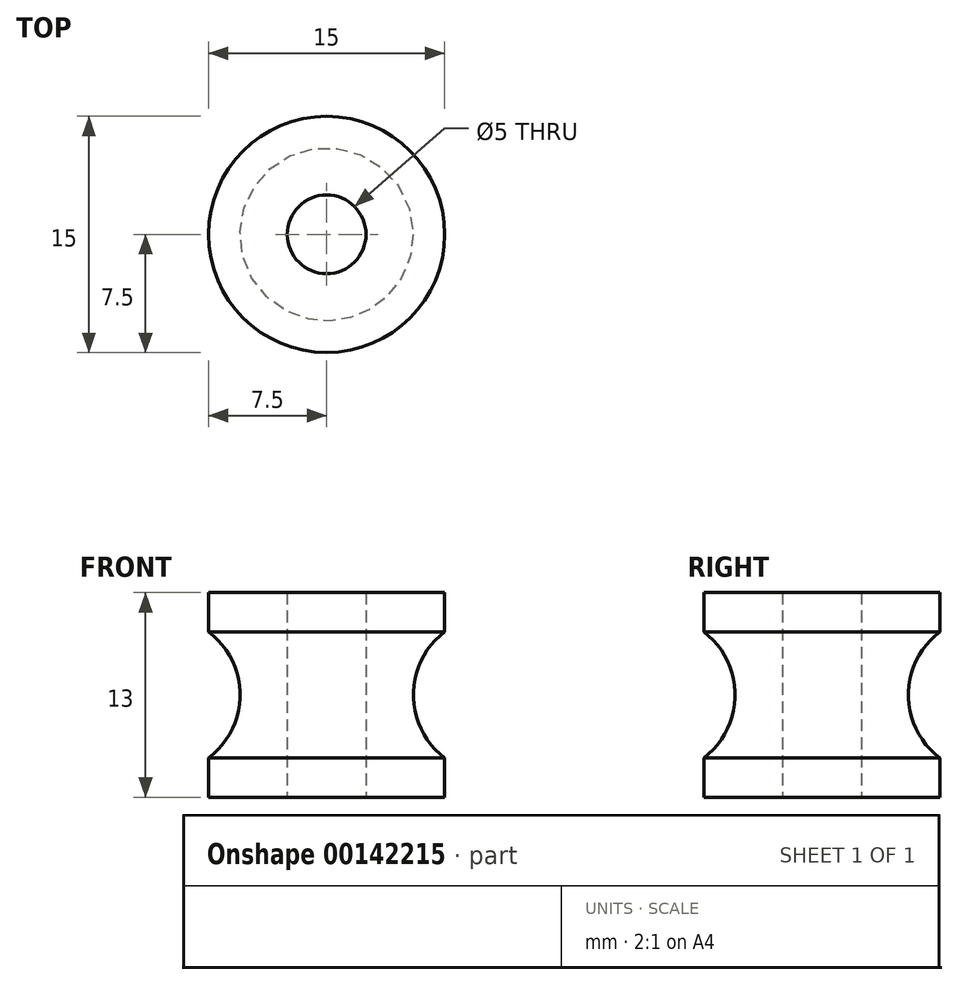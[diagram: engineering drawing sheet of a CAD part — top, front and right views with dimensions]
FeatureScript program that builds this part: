
annotation { "Feature Type Name" : "Feature", "Feature Type Description" : "" }
export const myFeature = defineFeature(function(context is Context, id is Id, definition is map)
    precondition{}
    {
        {
            var Q0;
            Q0=qCreatedBy(makeId("Top.planeOp"),FACE);
            var sketch = newSketch(context, id + "F0", { "sketchPlane" : qUnion([Q0])});
            skCircle(sketch, "E0", {"center": v(0, 0) * mm, "radius": 7.5 * mm});
            skCircle(sketch, "E1", {"center": v(0, 0) * mm, "radius": 2.5 * mm});
            skSolve(sketch);
        }
        {
            var Q0;
            Q0=qSketchRegion(id+"F0",true);
            extrude(context, id + "F1", {"entities" : qUnion([Q0]), "depth" : 13 * mm});
        }
        {
            var Q0;
            Q0=qCreatedBy(makeId("Top.planeOp"),FACE);
            cPlane(context, id + "F2", {"entities" : qUnion([Q0]), "cplaneType" : CPlaneType.OFFSET, "offset" : 6.5 * mm, "width" : 150 * mm, "height" : 150 * mm});
        }
        {
            var Q0;
            Q0=qCreatedBy(id+"F2.planeOp",FACE);
            var sketch = newSketch(context, id + "F3", { "sketchPlane" : qUnion([Q0])});
            skCircle(sketch, "E2", {"center": v(0, 0) * mm, "radius": 5.5 * mm});
            skSolve(sketch);
        }
        {
            var Q0;
            Q0=qCreatedBy(makeId("Top.planeOp"),FACE);
            cPlane(context, id + "F4", {"entities" : qUnion([Q0]), "cplaneType" : CPlaneType.OFFSET, "offset" : 2.5 * mm, "width" : 150 * mm, "height" : 150 * mm});
        }
        {
            var Q0;
            Q0=qCreatedBy(id+"F4.planeOp",FACE);
            var sketch = newSketch(context, id + "F5", { "sketchPlane" : qUnion([Q0])});
            skCircle(sketch, "E3.0", {"center": v(0, 0) * mm, "radius": 7.5 * mm});
            skSolve(sketch);
        }
        {
            var Q0;
            Q0=makeQuery(id+"F1.opExtrude","CAP_FACE",FACE,{"disambiguationData":[OSD([sQuery(id+"F0.wireOp",EDGE,"E0"),sQuery(id+"F0.wireOp",EDGE,"E1")])],"isStart":false});
            cPlane(context, id + "F6", {"entities" : qUnion([Q0]), "cplaneType" : CPlaneType.OFFSET, "offset" : 2.5 * mm, "oppositeDirection" : true, "width" : 150 * mm, "height" : 150 * mm});
        }
        {
            var Q0;
            Q0=qCreatedBy(id+"F6.planeOp",FACE);
            var sketch = newSketch(context, id + "F7", { "sketchPlane" : qUnion([Q0])});
            skCircle(sketch, "E4.0", {"center": v(0, 0) * mm, "radius": 7.5 * mm});
            skSolve(sketch);
        }
        {
            var Q0;
            Q0=qCreatedBy(makeId("Front.planeOp"),FACE);
            var sketch = newSketch(context, id + "F8", { "sketchPlane" : qUnion([Q0])});
            skLineSegment(sketch, "E5.0", {"start": v(-7.5, 10.5) * mm, "end": v(7.5, 10.5) * mm, "construction": true});
            skLineSegment(sketch, "E6.0", {"start": v(-5.5, 6.5) * mm, "end": v(5.5, 6.5) * mm, "construction": true});
            skLineSegment(sketch, "E7.0", {"start": v(-7.5, 2.5) * mm, "end": v(7.5, 2.5) * mm, "construction": true});
            skArc(sketch, "E8", {"start": v(7.5, 10.5) * mm, "mid": v(5.5, 6.5) * mm, "end": v(7.5, 2.5) * mm});
            skLineSegment(sketch, "E9", {"start": v(7.5, 10.5) * mm, "end": v(7.5, 2.5) * mm});
            skSolve(sketch);
        }
        {
            var Q0;
            Q0=qSketchRegion(id+"F8",true);
            var Q1;
            Q1=qConstructionFilter(qBodyType(qCreatedBy(id+"F3",EDGE),BodyType.WIRE),ConstructionObject.NO);
            sweep(context, id + "F9", {"operationType" : NewBodyOperationType.REMOVE, "profiles" : qUnion([Q0]), "path" : qUnion([Q1])});
        }
    });
